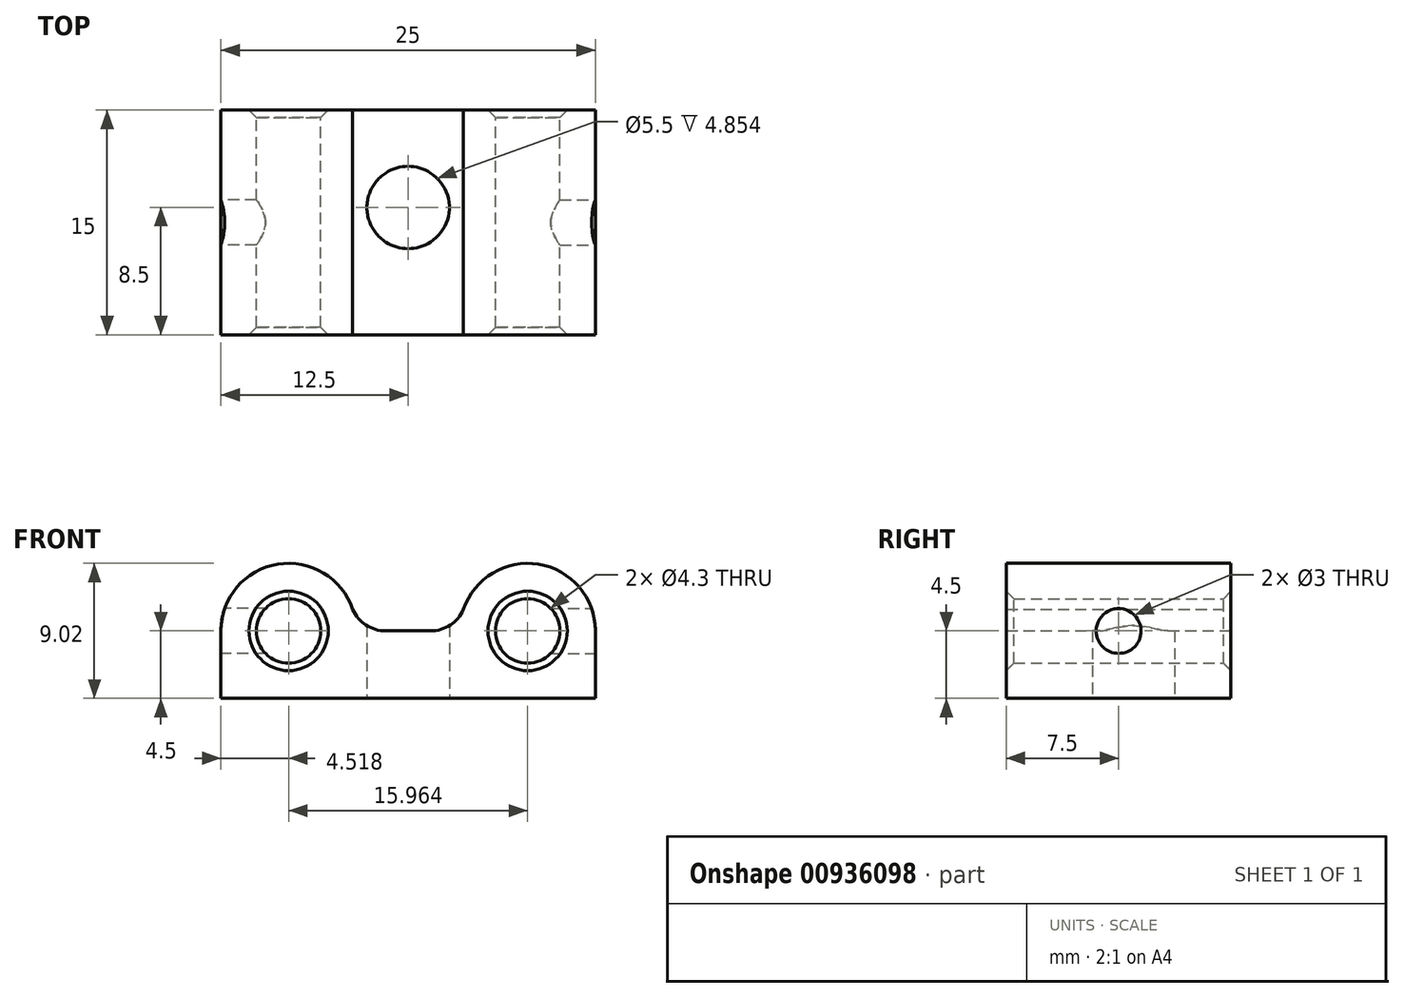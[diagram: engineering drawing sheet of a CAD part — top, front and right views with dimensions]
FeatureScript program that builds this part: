
annotation { "Feature Type Name" : "Feature", "Feature Type Description" : "" }
export const myFeature = defineFeature(function(context is Context, id is Id, definition is map)
    precondition{}
    {
        {
            var Q0;
            Q0=qCreatedBy(makeId("Front.planeOp"),FACE);
            var sketch = newSketch(context, id + "F0", { "sketchPlane" : qUnion([Q0])});
            skLineSegment(sketch, "E0", {"start": v(0, 13.86) * mm, "end": v(0, -11.4) * mm, "construction": true});
            skLineSegment(sketch, "E1", {"start": v(-12.5, 0) * mm, "end": v(0, 0) * mm});
            skLineSegment(sketch, "E2", {"start": v(-12.5, 0) * mm, "end": v(-12.5, 4.5) * mm});
            skArc(sketch, "E3", {"start": v(-3.7, 5.94) * mm, "mid": v(-8.71, 8.96) * mm, "end": v(-12.5, 4.5) * mm});
            skLineSegment(sketch, "E4", {"start": v(0, 4.5) * mm, "end": v(-1.5, 4.5) * mm});
            skArc(sketch, "E5", {"start": v(-3.7, 5.94) * mm, "mid": v(-2.81, 4.9) * mm, "end": v(-1.5, 4.5) * mm});
            skCircle(sketch, "E6", {"center": v(-7.98, 4.5) * mm, "radius": 2.15 * mm});
            skLineSegment(sketch, "E7.MirrorCS", {"start": v(0, 4.5) * mm, "end": v(1.5, 4.5) * mm});
            skLineSegment(sketch, "E8.MirrorCS", {"start": v(12.5, 0) * mm, "end": v(12.5, 4.5) * mm});
            skLineSegment(sketch, "E9.MirrorCS", {"start": v(12.5, 0) * mm, "end": v(0, 0) * mm});
            skCircle(sketch, "E10.MirrorC", {"center": v(7.98, 4.5) * mm, "radius": 2.15 * mm});
            skArc(sketch, "E11.MirrorCS", {"start": v(3.7, 5.94) * mm, "mid": v(2.81, 4.9) * mm, "end": v(1.5, 4.5) * mm});
            skArc(sketch, "E12.MirrorCS", {"start": v(3.7, 5.94) * mm, "mid": v(8.71, 8.96) * mm, "end": v(12.5, 4.5) * mm});
            skSolve(sketch);
        }
        {
            var Q0;
            Q0=makeQuery(id+"F0.imprint","IMPRINT",FACE,{"disambiguationData":[TD([[makeQuery(id+"F0.imprint","IMPRINT",EDGE,{"derivedFrom":sQuery(id+"F0.wireOp",EDGE,"E1")}),1.0]])]});
            extrude(context, id + "F1", {"entities" : qUnion([Q0]), "depth" : 15 * mm, "offsetDistance" : 25 * mm});
        }
        {
            var Q0;
            Q0=makeQuery(id+"F1.opExtrude","SWEPT_FACE",FACE,{"disambiguationData":[OSD([sQuery(id+"F0.wireOp",EDGE,"E1"),sQuery(id+"F0.wireOp",EDGE,"E9.MirrorCS")])]});
            var sketch = newSketch(context, id + "F2", { "sketchPlane" : qUnion([Q0])});
            skPoint(sketch, "E13", {"position": v(0, 6.5) * mm});
            skSolve(sketch);
        }
        {
            var Q0;
            Q0=sQuery(id+"F2.wireOp",VERTEX,"E13");
            var Q1;
            Q1=makeQuery(id+"F1.opExtrude","SWEPT_BODY",BODY,{"disambiguationData":[OSD([sQuery(id+"F0.wireOp",EDGE,"E1"),sQuery(id+"F0.wireOp",EDGE,"E2"),sQuery(id+"F0.wireOp",EDGE,"E3"),sQuery(id+"F0.wireOp",EDGE,"E4"),sQuery(id+"F0.wireOp",EDGE,"E5"),sQuery(id+"F0.wireOp",EDGE,"E6"),sQuery(id+"F0.wireOp",EDGE,"E7.MirrorCS"),sQuery(id+"F0.wireOp",EDGE,"E8.MirrorCS"),sQuery(id+"F0.wireOp",EDGE,"E9.MirrorCS"),sQuery(id+"F0.wireOp",EDGE,"E10.MirrorC"),sQuery(id+"F0.wireOp",EDGE,"E11.MirrorCS"),sQuery(id+"F0.wireOp",EDGE,"E12.MirrorCS")])]});
            hole(context, id + "F3", {"style" : HoleStyle.SIMPLE, "endStyle" : HoleEndStyle.THROUGH, "holeDiameter" : 5.5 * mm, "majorDiameter" : 5 * mm, "isTappedThrough" : true, "tappedDepth" : 12 * mm, "tapClearance" : 3, "startFromSketch" : true, "locations" : qUnion([Q0]), "scope" : qUnion([Q1])});
        }
        {
            var Q0;
            Q0=makeQuery(id+"F1.opExtrude","CAP_EDGE",EDGE,{"disambiguationData":[OSD([sQuery(id+"F0.wireOp",EDGE,"E6")])],"isStart":true});
            var Q1;
            Q1=makeQuery(id+"F1.opExtrude","CAP_EDGE",EDGE,{"disambiguationData":[OSD([sQuery(id+"F0.wireOp",EDGE,"E10.MirrorC")])],"isStart":true});
            var Q2;
            Q2=makeQuery(id+"F1.opExtrude","CAP_EDGE",EDGE,{"disambiguationData":[OSD([sQuery(id+"F0.wireOp",EDGE,"E6")])],"isStart":false});
            var Q3;
            Q3=makeQuery(id+"F1.opExtrude","CAP_EDGE",EDGE,{"disambiguationData":[OSD([sQuery(id+"F0.wireOp",EDGE,"E10.MirrorC")])],"isStart":false});
            var Q4;
            Q4=makeQuery(id+"F3.hole-0.boolean.opBoolean","COPY",EDGE,{"derivedFrom":makeQuery(id+"F3.hole-0.opRevolve","SWEPT_EDGE",EDGE,{"disambiguationData":[OSD([sQuery(id+"F3.hole-0.sketch.wireOp",EDGE,"core_line_2"),sQuery(id+"F3.hole-0.sketch.wireOp",EDGE,"core_line_3")])]})});
            chamfer(context, id + "F4", {"entities" : qUnion([Q0, Q1, Q2, Q3, Q4]), "width" : 0.5 * mm, "tangentPropagation" : true});
        }
        {
            var Q0;
            Q0=makeQuery(id+"F1.opExtrude","SWEPT_FACE",FACE,{"disambiguationData":[OSD([sQuery(id+"F0.wireOp",EDGE,"E2")])]});
            var sketch = newSketch(context, id + "F5", { "sketchPlane" : qUnion([Q0])});
            skPoint(sketch, "E14", {"position": v(7.5, 4.5) * mm});
            skSolve(sketch);
        }
        {
            var Q0;
            Q0=sQuery(id+"F5.wireOp",VERTEX,"E14");
            var Q1;
            Q1=makeQuery(id+"F1.opExtrude","SWEPT_BODY",BODY,{"disambiguationData":[OSD([sQuery(id+"F0.wireOp",EDGE,"E1"),sQuery(id+"F0.wireOp",EDGE,"E2"),sQuery(id+"F0.wireOp",EDGE,"E3"),sQuery(id+"F0.wireOp",EDGE,"E4"),sQuery(id+"F0.wireOp",EDGE,"E5"),sQuery(id+"F0.wireOp",EDGE,"E6"),sQuery(id+"F0.wireOp",EDGE,"E7.MirrorCS"),sQuery(id+"F0.wireOp",EDGE,"E8.MirrorCS"),sQuery(id+"F0.wireOp",EDGE,"E9.MirrorCS"),sQuery(id+"F0.wireOp",EDGE,"E10.MirrorC"),sQuery(id+"F0.wireOp",EDGE,"E11.MirrorCS"),sQuery(id+"F0.wireOp",EDGE,"E12.MirrorCS")])]});
            hole(context, id + "F6", {"style" : HoleStyle.SIMPLE, "endStyle" : HoleEndStyle.BLIND, "holeDiameter" : 3 * mm, "majorDiameter" : 5 * mm, "holeDepth" : 3 * mm, "isTappedThrough" : true, "tappedDepth" : 12 * mm, "tapClearance" : 3, "startFromSketch" : true, "locations" : qUnion([Q0]), "scope" : qUnion([Q1])});
        }
        {
            var Q0;
            Q0=makeQuery(id+"F1.opExtrude","SWEPT_FACE",FACE,{"disambiguationData":[OSD([sQuery(id+"F0.wireOp",EDGE,"E8.MirrorCS")])]});
            var sketch = newSketch(context, id + "F7", { "sketchPlane" : qUnion([Q0])});
            skPoint(sketch, "E15", {"position": v(-7.5, 4.5) * mm});
            skSolve(sketch);
        }
        {
            var Q0;
            Q0=sQuery(id+"F7.wireOp",VERTEX,"E15");
            var Q1;
            Q1=makeQuery(id+"F1.opExtrude","SWEPT_BODY",BODY,{"disambiguationData":[OSD([sQuery(id+"F0.wireOp",EDGE,"E1"),sQuery(id+"F0.wireOp",EDGE,"E2"),sQuery(id+"F0.wireOp",EDGE,"E3"),sQuery(id+"F0.wireOp",EDGE,"E4"),sQuery(id+"F0.wireOp",EDGE,"E5"),sQuery(id+"F0.wireOp",EDGE,"E6"),sQuery(id+"F0.wireOp",EDGE,"E7.MirrorCS"),sQuery(id+"F0.wireOp",EDGE,"E8.MirrorCS"),sQuery(id+"F0.wireOp",EDGE,"E9.MirrorCS"),sQuery(id+"F0.wireOp",EDGE,"E10.MirrorC"),sQuery(id+"F0.wireOp",EDGE,"E11.MirrorCS"),sQuery(id+"F0.wireOp",EDGE,"E12.MirrorCS")])]});
            hole(context, id + "F8", {"style" : HoleStyle.SIMPLE, "endStyle" : HoleEndStyle.BLIND, "holeDiameter" : 3 * mm, "majorDiameter" : 5 * mm, "holeDepth" : 3 * mm, "isTappedThrough" : true, "tappedDepth" : 12 * mm, "tapClearance" : 3, "startFromSketch" : true, "locations" : qUnion([Q0]), "scope" : qUnion([Q1])});
        }
    });
